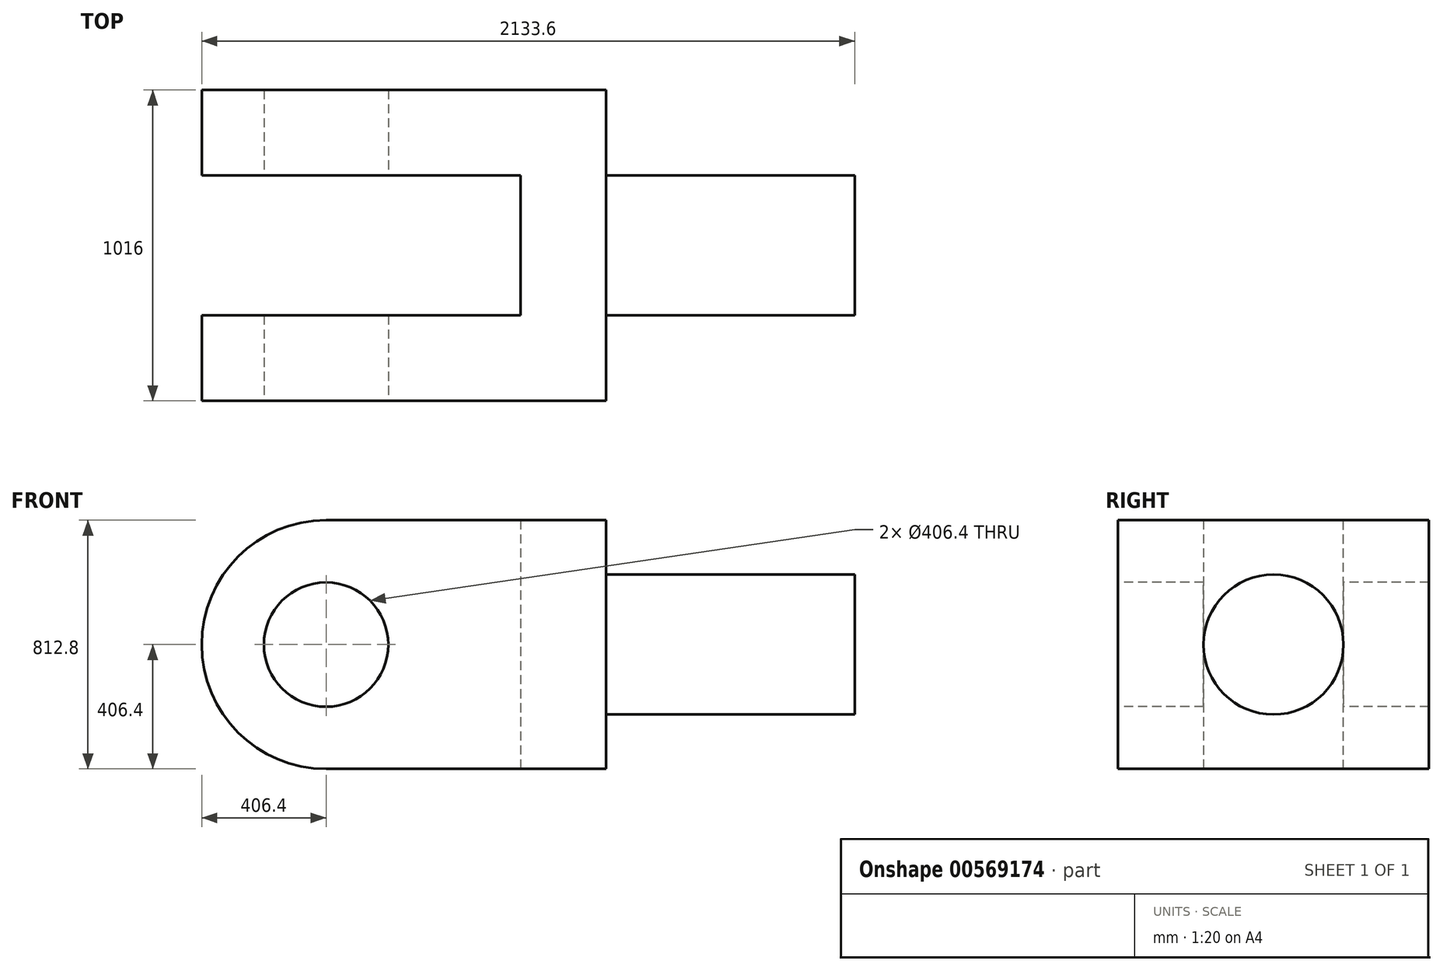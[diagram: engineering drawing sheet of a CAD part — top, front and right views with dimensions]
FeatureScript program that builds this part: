
annotation { "Feature Type Name" : "Feature", "Feature Type Description" : "" }
export const myFeature = defineFeature(function(context is Context, id is Id, definition is map)
    precondition{}
    {
        {
            var Q0;
            Q0=qCreatedBy(makeId("Top.planeOp"),FACE);
            var sketch = newSketch(context, id + "F0", { "sketchPlane" : qUnion([Q0])});
            skLineSegment(sketch, "E0", {"start": v(0, 0) * mm, "end": v(0, 736.6) * mm});
            skLineSegment(sketch, "E1", {"start": v(0, 736.6) * mm, "end": v(-1320.8, 736.6) * mm});
            skLineSegment(sketch, "E2", {"start": v(-1320.8, 736.6) * mm, "end": v(-1320.8, 457.2) * mm});
            skLineSegment(sketch, "E3", {"start": v(-1320.8, 457.2) * mm, "end": v(-279.4, 457.2) * mm});
            skLineSegment(sketch, "E4", {"start": v(-279.4, 457.2) * mm, "end": v(-279.4, 0) * mm});
            skLineSegment(sketch, "E5", {"start": v(-279.4, 0) * mm, "end": v(-1320.8, 0) * mm});
            skLineSegment(sketch, "E6", {"start": v(-1320.8, 0) * mm, "end": v(-1320.8, -279.4) * mm});
            skLineSegment(sketch, "E7", {"start": v(-1320.8, -279.4) * mm, "end": v(0, -279.4) * mm});
            skLineSegment(sketch, "E8", {"start": v(0, -279.4) * mm, "end": v(0, 0) * mm});
            skSolve(sketch);
        }
        {
            var Q0;
            Q0 = qSketchRegion(id + "F0", true);
            var Q1;
            Q1 = qSketchRegion(id + "F2", true);
            extrude(context, id + "F1", {"entities" : qUnion([Q0, Q1]), "depth" : 812.8 * mm, "offsetDistance" : 25.4 * mm});
        }
        {
            var Q0;
            Q0=makeQuery(id+"F1.opExtrude","SWEPT_FACE",FACE,{"disambiguationData":[OSD([sQuery(id+"F0.wireOp",EDGE,"E7")])]});
            var sketch = newSketch(context, id + "F2", { "sketchPlane" : qUnion([Q0])});
            skCircle(sketch, "E9", {"center": v(-914.4, 406.4) * mm, "radius": 203.2 * mm});
            skPoint(sketch, "E9.centerSnap0", {"position": v(-1320.8, 406.4) * mm});
            skArc(sketch, "E10", {"start": v(-914.4, 812.8) * mm, "mid": v(-1320.8, 406.4) * mm, "end": v(-914.4, 0) * mm});
            skSolve(sketch);
        }
        {
            var Q0;
            {var subQ0=sQuery(id+"F2.wireOp",EDGE,"E10");Q0=makeQuery(id+"F2.imprint","IMPRINT",FACE,{"disambiguationData":[TD([[makeQuery(id+"F2.imprint","IMPRINT",EDGE,{"derivedFrom":subQ0}),-1.0]])]});}
            var Q1;
            Q1=makeQuery(id+"F2.imprint","IMPRINT",FACE,{"disambiguationData":[TD([[makeQuery(id+"F2.imprint","IMPRINT",EDGE,{"derivedFrom":sQuery(id+"F2.wireOp",EDGE,"E9")}),1.0]])]});
            extrude(context, id + "F3", {"entities" : qUnion([Q0, Q1]), "operationType" : NewBodyOperationType.REMOVE, "endBound" : BoundingType.THROUGH_ALL, "oppositeDirection" : true, "depth" : 25.4 * mm, "offsetDistance" : 25.4 * mm});
        }
        {
            var Q0;
            Q0=makeQuery(id+"F1.opExtrude","SWEPT_FACE",FACE,{"disambiguationData":[OSD([sQuery(id+"F0.wireOp",EDGE,"E0"),sQuery(id+"F0.wireOp",EDGE,"E8")])]});
            var sketch = newSketch(context, id + "F4", { "sketchPlane" : qUnion([Q0])});
            skCircle(sketch, "E11", {"center": v(228.6, 406.4) * mm, "radius": 228.6 * mm});
            skPoint(sketch, "E11.centerSnap0", {"position": v(-279.4, 406.4) * mm});
            skPoint(sketch, "E11.centerSnap1", {"position": v(228.6, 812.8) * mm});
            skSolve(sketch);
        }
        {
            var Q0;
            Q0=makeQuery(id+"F4.imprint","IMPRINT",FACE,{"disambiguationData":[TD([[makeQuery(id+"F4.imprint","IMPRINT",EDGE,{"derivedFrom":sQuery(id+"F4.wireOp",EDGE,"E11")}),1.0]])]});
            extrude(context, id + "F5", {"entities" : qUnion([Q0]), "operationType" : NewBodyOperationType.ADD, "depth" : 812.8 * mm, "offsetDistance" : 25.4 * mm});
        }
    });
